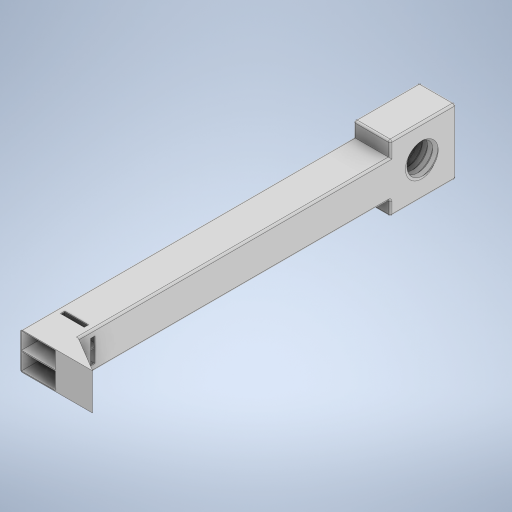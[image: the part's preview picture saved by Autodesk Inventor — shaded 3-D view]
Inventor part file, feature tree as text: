
AUTODESK INVENTOR PART (.ipt)
format: ipt  version: 2024 (Build 280153000, 153)  size: 531,456 bytes
history: native  units: mm
features: sketch x11, extrude x10, other x1, fillet x1
ambient origin geometry x8: Origin, YZ Plane, XZ Plane, XY Plane, X Axis, Y Axis, Z Axis, Center Point
bodies: Volumenkörper1 (feature_tree)
feature tree (23):
  extrude  "Extrusion1"  Depth=10.0mm
  extrude  "Extrusion2"  Depth=10.0mm
  extrude  "Extrusion3"  Depth=18.0mm TaperAngle=0.0deg
  extrude  "Extrusion4"  Depth=10.0mm TaperAngle=0.0deg
  other  "Spirale1"
  extrude  "Extrusion6"  Depth=9.0mm TaperAngle=0.0deg
  extrude  "Extrusion7"  Depth=10.0mm
  extrude  "Extrusion8"  Depth=0.2mm
  extrude  "Extrusion9"  Depth=9.5mm
  fillet  "Rundung2"  Radius=9.5mm
  extrude  "Extrusion10"  Depth=1.5mm
  extrude  "Extrusion11"  Depth=0.5mm
  sketch  "Skizze1"  dims[d0=10.0mm d1=10.0mm]
  sketch  "Skizze2"  dims[d2=91.0mm d3=0.0mm d4=10.0mm]
  sketch  "Skizze3"  dims[d5=18.0mm d6=18.0mm d7=0.0mm]
  sketch  "Skizze4"  dims[d8=10.0mm d9=9.0mm d10=0.0mm]
  sketch  "Skizze5"  dims[d17=7.2mm d18=9.0mm d19=0.0mm]
  sketch  "Skizze7"  dims[d22=1.4mm d23=11.0mm d24=10.0mm d25=0.0mm d26=90.0deg d27=90.0deg d28=0.0mm d29=0.0mm d33=1.7mm]
  sketch  "Skizze8"  dims[d34=60.0deg d35=0.2mm]
  sketch  "Skizze9"  dims[d36=1.0mm d37=0.0mm d39=9.5mm d40=9.5mm]
  sketch  "Skizze10"  dims[d41=9.75mm d42=0.0mm d43=1.5mm]
  sketch  "Skizze11"  dims[d44=1.5mm d45=0.5mm]
  sketch  "Skizze14"  dims[d46=0.5mm d47=1.5mm d48=1.5mm d49=1.5mm d50=1.5mm d51=0.5mm d52=0.5mm d53=1.2mm d54=0.0mm d55=2.0mm d56=0.0mm d57=0.5mm d59=0.5mm d60=10.0mm d61=0.0mm d62=0.0mm d63=0.0mm d64=0.15mm d65=0.15mm d66=11.75mm d67=0.0mm d38=0.0mm]
